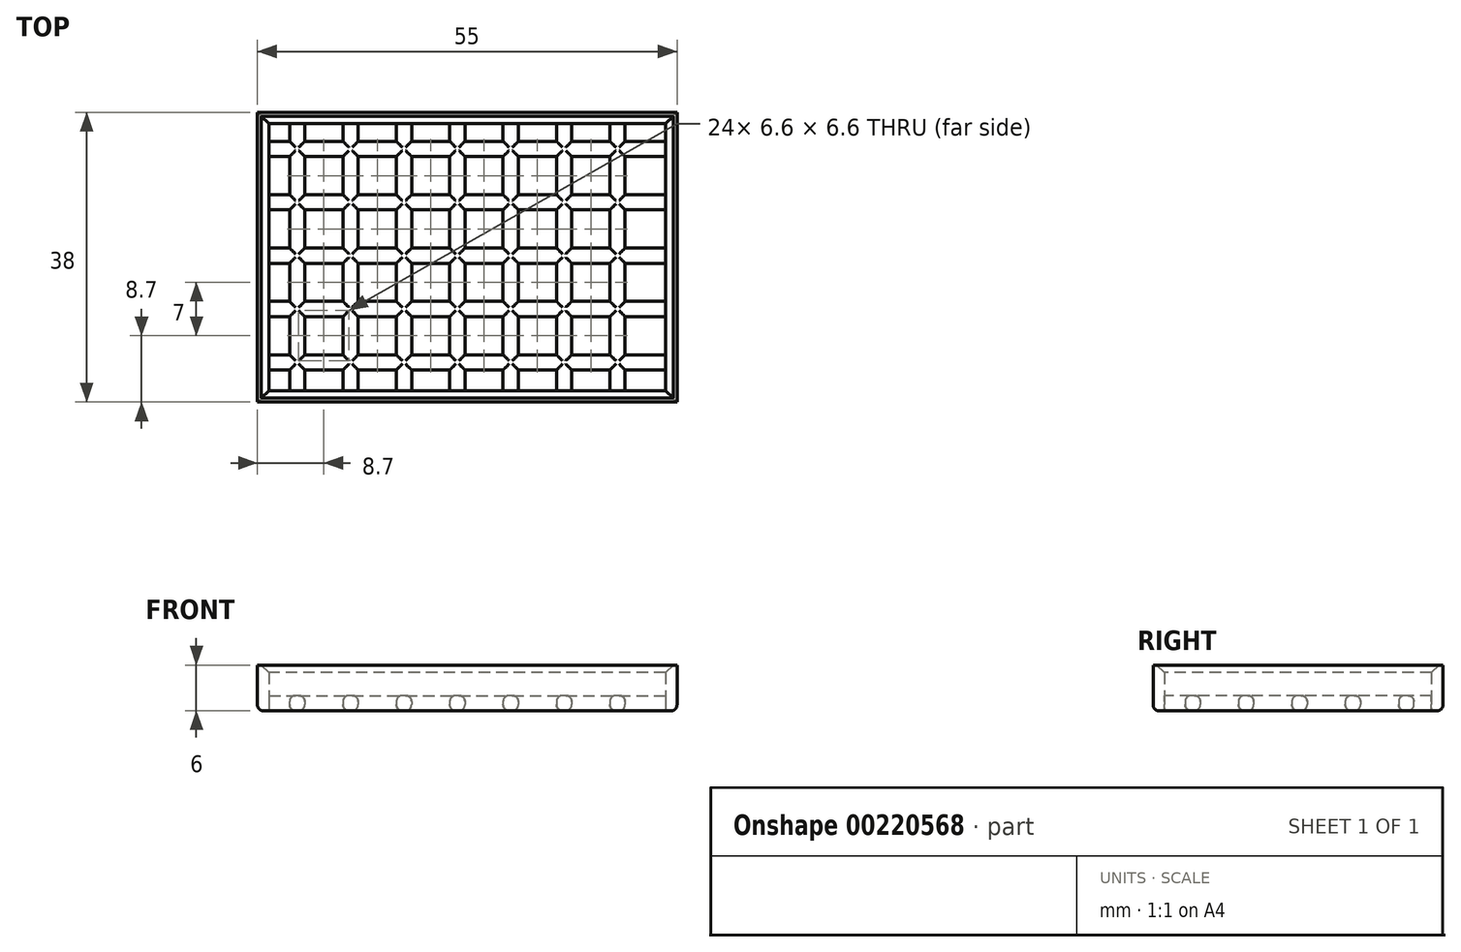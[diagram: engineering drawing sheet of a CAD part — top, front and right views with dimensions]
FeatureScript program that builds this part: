
annotation { "Feature Type Name" : "Feature", "Feature Type Description" : "" }
export const myFeature = defineFeature(function(context is Context, id is Id, definition is map)
    precondition{}
    {
        {
            var Q0;
            Q0=qCreatedBy(makeId("Top.planeOp"),FACE);
            var sketch = newSketch(context, id + "F0", { "sketchPlane" : qUnion([Q0])});
            skLineSegment(sketch, "E0.bottom", {"start": v(0, 38) * mm, "end": v(55, 38) * mm});
            skLineSegment(sketch, "E0.top", {"start": v(0, 0) * mm, "end": v(55, 0) * mm});
            skLineSegment(sketch, "E0.left", {"start": v(0, 38) * mm, "end": v(0, 0) * mm});
            skLineSegment(sketch, "E0.right", {"start": v(55, 38) * mm, "end": v(55, 0) * mm});
            skSolve(sketch);
        }
        {
            var Q0;
            Q0=qSketchRegion(id+"F0",true);
            extrude(context, id + "F1", {"entities" : qUnion([Q0]), "oppositeDirection" : true, "depth" : 2 * mm});
        }
        {
            var Q0;
            Q0=makeQuery(id+"F1.opExtrude","CAP_FACE",FACE,{"disambiguationData":[OSD([sQuery(id+"F0.wireOp",EDGE,"E0.bottom"),sQuery(id+"F0.wireOp",EDGE,"E0.top"),sQuery(id+"F0.wireOp",EDGE,"E0.left"),sQuery(id+"F0.wireOp",EDGE,"E0.right")])],"isStart":true});
            var sketch = newSketch(context, id + "F2", { "sketchPlane" : qUnion([Q0])});
            skLineSegment(sketch, "E1.bottom", {"start": v(-0.8, 39.2) * mm, "end": v(4.2, 39.2) * mm});
            skLineSegment(sketch, "E1.top", {"start": v(-0.8, 34.2) * mm, "end": v(4.2, 34.2) * mm});
            skLineSegment(sketch, "E1.left", {"start": v(-0.8, 39.2) * mm, "end": v(-0.8, 34.2) * mm});
            skLineSegment(sketch, "E1.right", {"start": v(4.2, 39.2) * mm, "end": v(4.2, 34.2) * mm});
            skLineSegment(sketch, "E2.0.1.0", {"start": v(-0.8, 32.2) * mm, "end": v(4.2, 32.2) * mm});
            skLineSegment(sketch, "E2.0.1.1", {"start": v(-0.8, 27.2) * mm, "end": v(4.2, 27.2) * mm});
            skLineSegment(sketch, "E2.0.1.2", {"start": v(-0.8, 32.2) * mm, "end": v(-0.8, 27.2) * mm});
            skLineSegment(sketch, "E2.0.1.3", {"start": v(4.2, 32.2) * mm, "end": v(4.2, 27.2) * mm});
            skLineSegment(sketch, "E2.0.2.0", {"start": v(-0.8, 25.2) * mm, "end": v(4.2, 25.2) * mm});
            skLineSegment(sketch, "E2.0.2.1", {"start": v(-0.8, 20.2) * mm, "end": v(4.2, 20.2) * mm});
            skLineSegment(sketch, "E2.0.2.2", {"start": v(-0.8, 25.2) * mm, "end": v(-0.8, 20.2) * mm});
            skLineSegment(sketch, "E2.0.2.3", {"start": v(4.2, 25.2) * mm, "end": v(4.2, 20.2) * mm});
            skLineSegment(sketch, "E2.0.3.0", {"start": v(-0.8, 18.2) * mm, "end": v(4.2, 18.2) * mm});
            skLineSegment(sketch, "E2.0.3.1", {"start": v(-0.8, 13.2) * mm, "end": v(4.2, 13.2) * mm});
            skLineSegment(sketch, "E2.0.3.2", {"start": v(-0.8, 18.2) * mm, "end": v(-0.8, 13.2) * mm});
            skLineSegment(sketch, "E2.0.3.3", {"start": v(4.2, 18.2) * mm, "end": v(4.2, 13.2) * mm});
            skLineSegment(sketch, "E2.0.4.0", {"start": v(-0.8, 11.2) * mm, "end": v(4.2, 11.2) * mm});
            skLineSegment(sketch, "E2.0.4.1", {"start": v(-0.8, 6.2) * mm, "end": v(4.2, 6.2) * mm});
            skLineSegment(sketch, "E2.0.4.2", {"start": v(-0.8, 11.2) * mm, "end": v(-0.8, 6.2) * mm});
            skLineSegment(sketch, "E2.0.4.3", {"start": v(4.2, 11.2) * mm, "end": v(4.2, 6.2) * mm});
            skLineSegment(sketch, "E2.0.5.0", {"start": v(-0.8, 4.2) * mm, "end": v(4.2, 4.2) * mm});
            skLineSegment(sketch, "E2.0.5.1", {"start": v(-0.8, -0.8) * mm, "end": v(4.2, -0.8) * mm});
            skLineSegment(sketch, "E2.0.5.2", {"start": v(-0.8, 4.2) * mm, "end": v(-0.8, -0.8) * mm});
            skLineSegment(sketch, "E2.0.5.3", {"start": v(4.2, 4.2) * mm, "end": v(4.2, -0.8) * mm});
            skLineSegment(sketch, "E2.1.0.0", {"start": v(6.2, 39.2) * mm, "end": v(11.2, 39.2) * mm});
            skLineSegment(sketch, "E2.1.0.1", {"start": v(6.2, 34.2) * mm, "end": v(11.2, 34.2) * mm});
            skLineSegment(sketch, "E2.1.0.2", {"start": v(6.2, 39.2) * mm, "end": v(6.2, 34.2) * mm});
            skLineSegment(sketch, "E2.1.0.3", {"start": v(11.2, 39.2) * mm, "end": v(11.2, 34.2) * mm});
            skLineSegment(sketch, "E2.1.1.0", {"start": v(6.2, 32.2) * mm, "end": v(11.2, 32.2) * mm});
            skLineSegment(sketch, "E2.1.1.1", {"start": v(6.2, 27.2) * mm, "end": v(11.2, 27.2) * mm});
            skLineSegment(sketch, "E2.1.1.2", {"start": v(6.2, 32.2) * mm, "end": v(6.2, 27.2) * mm});
            skLineSegment(sketch, "E2.1.1.3", {"start": v(11.2, 32.2) * mm, "end": v(11.2, 27.2) * mm});
            skLineSegment(sketch, "E2.1.2.0", {"start": v(6.2, 25.2) * mm, "end": v(11.2, 25.2) * mm});
            skLineSegment(sketch, "E2.1.2.1", {"start": v(6.2, 20.2) * mm, "end": v(11.2, 20.2) * mm});
            skLineSegment(sketch, "E2.1.2.2", {"start": v(6.2, 25.2) * mm, "end": v(6.2, 20.2) * mm});
            skLineSegment(sketch, "E2.1.2.3", {"start": v(11.2, 25.2) * mm, "end": v(11.2, 20.2) * mm});
            skLineSegment(sketch, "E2.1.3.0", {"start": v(6.2, 18.2) * mm, "end": v(11.2, 18.2) * mm});
            skLineSegment(sketch, "E2.1.3.1", {"start": v(6.2, 13.2) * mm, "end": v(11.2, 13.2) * mm});
            skLineSegment(sketch, "E2.1.3.2", {"start": v(6.2, 18.2) * mm, "end": v(6.2, 13.2) * mm});
            skLineSegment(sketch, "E2.1.3.3", {"start": v(11.2, 18.2) * mm, "end": v(11.2, 13.2) * mm});
            skLineSegment(sketch, "E2.1.4.0", {"start": v(6.2, 11.2) * mm, "end": v(11.2, 11.2) * mm});
            skLineSegment(sketch, "E2.1.4.1", {"start": v(6.2, 6.2) * mm, "end": v(11.2, 6.2) * mm});
            skLineSegment(sketch, "E2.1.4.2", {"start": v(6.2, 11.2) * mm, "end": v(6.2, 6.2) * mm});
            skLineSegment(sketch, "E2.1.4.3", {"start": v(11.2, 11.2) * mm, "end": v(11.2, 6.2) * mm});
            skLineSegment(sketch, "E2.1.5.0", {"start": v(6.2, 4.2) * mm, "end": v(11.2, 4.2) * mm});
            skLineSegment(sketch, "E2.1.5.1", {"start": v(6.2, -0.8) * mm, "end": v(11.2, -0.8) * mm});
            skLineSegment(sketch, "E2.1.5.2", {"start": v(6.2, 4.2) * mm, "end": v(6.2, -0.8) * mm});
            skLineSegment(sketch, "E2.1.5.3", {"start": v(11.2, 4.2) * mm, "end": v(11.2, -0.8) * mm});
            skLineSegment(sketch, "E2.2.0.0", {"start": v(13.2, 39.2) * mm, "end": v(18.2, 39.2) * mm});
            skLineSegment(sketch, "E2.2.0.1", {"start": v(13.2, 34.2) * mm, "end": v(18.2, 34.2) * mm});
            skLineSegment(sketch, "E2.2.0.2", {"start": v(13.2, 39.2) * mm, "end": v(13.2, 34.2) * mm});
            skLineSegment(sketch, "E2.2.0.3", {"start": v(18.2, 39.2) * mm, "end": v(18.2, 34.2) * mm});
            skLineSegment(sketch, "E2.2.1.0", {"start": v(13.2, 32.2) * mm, "end": v(18.2, 32.2) * mm});
            skLineSegment(sketch, "E2.2.1.1", {"start": v(13.2, 27.2) * mm, "end": v(18.2, 27.2) * mm});
            skLineSegment(sketch, "E2.2.1.2", {"start": v(13.2, 32.2) * mm, "end": v(13.2, 27.2) * mm});
            skLineSegment(sketch, "E2.2.1.3", {"start": v(18.2, 32.2) * mm, "end": v(18.2, 27.2) * mm});
            skLineSegment(sketch, "E2.2.2.0", {"start": v(13.2, 25.2) * mm, "end": v(18.2, 25.2) * mm});
            skLineSegment(sketch, "E2.2.2.1", {"start": v(13.2, 20.2) * mm, "end": v(18.2, 20.2) * mm});
            skLineSegment(sketch, "E2.2.2.2", {"start": v(13.2, 25.2) * mm, "end": v(13.2, 20.2) * mm});
            skLineSegment(sketch, "E2.2.2.3", {"start": v(18.2, 25.2) * mm, "end": v(18.2, 20.2) * mm});
            skLineSegment(sketch, "E2.2.3.0", {"start": v(13.2, 18.2) * mm, "end": v(18.2, 18.2) * mm});
            skLineSegment(sketch, "E2.2.3.1", {"start": v(13.2, 13.2) * mm, "end": v(18.2, 13.2) * mm});
            skLineSegment(sketch, "E2.2.3.2", {"start": v(13.2, 18.2) * mm, "end": v(13.2, 13.2) * mm});
            skLineSegment(sketch, "E2.2.3.3", {"start": v(18.2, 18.2) * mm, "end": v(18.2, 13.2) * mm});
            skLineSegment(sketch, "E2.2.4.0", {"start": v(13.2, 11.2) * mm, "end": v(18.2, 11.2) * mm});
            skLineSegment(sketch, "E2.2.4.1", {"start": v(13.2, 6.2) * mm, "end": v(18.2, 6.2) * mm});
            skLineSegment(sketch, "E2.2.4.2", {"start": v(13.2, 11.2) * mm, "end": v(13.2, 6.2) * mm});
            skLineSegment(sketch, "E2.2.4.3", {"start": v(18.2, 11.2) * mm, "end": v(18.2, 6.2) * mm});
            skLineSegment(sketch, "E2.2.5.0", {"start": v(13.2, 4.2) * mm, "end": v(18.2, 4.2) * mm});
            skLineSegment(sketch, "E2.2.5.1", {"start": v(13.2, -0.8) * mm, "end": v(18.2, -0.8) * mm});
            skLineSegment(sketch, "E2.2.5.2", {"start": v(13.2, 4.2) * mm, "end": v(13.2, -0.8) * mm});
            skLineSegment(sketch, "E2.2.5.3", {"start": v(18.2, 4.2) * mm, "end": v(18.2, -0.8) * mm});
            skLineSegment(sketch, "E2.3.0.0", {"start": v(20.2, 39.2) * mm, "end": v(25.2, 39.2) * mm});
            skLineSegment(sketch, "E2.3.0.1", {"start": v(20.2, 34.2) * mm, "end": v(25.2, 34.2) * mm});
            skLineSegment(sketch, "E2.3.0.2", {"start": v(20.2, 39.2) * mm, "end": v(20.2, 34.2) * mm});
            skLineSegment(sketch, "E2.3.0.3", {"start": v(25.2, 39.2) * mm, "end": v(25.2, 34.2) * mm});
            skLineSegment(sketch, "E2.3.1.0", {"start": v(20.2, 32.2) * mm, "end": v(25.2, 32.2) * mm});
            skLineSegment(sketch, "E2.3.1.1", {"start": v(20.2, 27.2) * mm, "end": v(25.2, 27.2) * mm});
            skLineSegment(sketch, "E2.3.1.2", {"start": v(20.2, 32.2) * mm, "end": v(20.2, 27.2) * mm});
            skLineSegment(sketch, "E2.3.1.3", {"start": v(25.2, 32.2) * mm, "end": v(25.2, 27.2) * mm});
            skLineSegment(sketch, "E2.3.2.0", {"start": v(20.2, 25.2) * mm, "end": v(25.2, 25.2) * mm});
            skLineSegment(sketch, "E2.3.2.1", {"start": v(20.2, 20.2) * mm, "end": v(25.2, 20.2) * mm});
            skLineSegment(sketch, "E2.3.2.2", {"start": v(20.2, 25.2) * mm, "end": v(20.2, 20.2) * mm});
            skLineSegment(sketch, "E2.3.2.3", {"start": v(25.2, 25.2) * mm, "end": v(25.2, 20.2) * mm});
            skLineSegment(sketch, "E2.3.3.0", {"start": v(20.2, 18.2) * mm, "end": v(25.2, 18.2) * mm});
            skLineSegment(sketch, "E2.3.3.1", {"start": v(20.2, 13.2) * mm, "end": v(25.2, 13.2) * mm});
            skLineSegment(sketch, "E2.3.3.2", {"start": v(20.2, 18.2) * mm, "end": v(20.2, 13.2) * mm});
            skLineSegment(sketch, "E2.3.3.3", {"start": v(25.2, 18.2) * mm, "end": v(25.2, 13.2) * mm});
            skLineSegment(sketch, "E2.3.4.0", {"start": v(20.2, 11.2) * mm, "end": v(25.2, 11.2) * mm});
            skLineSegment(sketch, "E2.3.4.1", {"start": v(20.2, 6.2) * mm, "end": v(25.2, 6.2) * mm});
            skLineSegment(sketch, "E2.3.4.2", {"start": v(20.2, 11.2) * mm, "end": v(20.2, 6.2) * mm});
            skLineSegment(sketch, "E2.3.4.3", {"start": v(25.2, 11.2) * mm, "end": v(25.2, 6.2) * mm});
            skLineSegment(sketch, "E2.3.5.0", {"start": v(20.2, 4.2) * mm, "end": v(25.2, 4.2) * mm});
            skLineSegment(sketch, "E2.3.5.1", {"start": v(20.2, -0.8) * mm, "end": v(25.2, -0.8) * mm});
            skLineSegment(sketch, "E2.3.5.2", {"start": v(20.2, 4.2) * mm, "end": v(20.2, -0.8) * mm});
            skLineSegment(sketch, "E2.3.5.3", {"start": v(25.2, 4.2) * mm, "end": v(25.2, -0.8) * mm});
            skLineSegment(sketch, "E2.4.0.0", {"start": v(27.2, 39.2) * mm, "end": v(32.2, 39.2) * mm});
            skLineSegment(sketch, "E2.4.0.1", {"start": v(27.2, 34.2) * mm, "end": v(32.2, 34.2) * mm});
            skLineSegment(sketch, "E2.4.0.2", {"start": v(27.2, 39.2) * mm, "end": v(27.2, 34.2) * mm});
            skLineSegment(sketch, "E2.4.0.3", {"start": v(32.2, 39.2) * mm, "end": v(32.2, 34.2) * mm});
            skLineSegment(sketch, "E2.4.1.0", {"start": v(27.2, 32.2) * mm, "end": v(32.2, 32.2) * mm});
            skLineSegment(sketch, "E2.4.1.1", {"start": v(27.2, 27.2) * mm, "end": v(32.2, 27.2) * mm});
            skLineSegment(sketch, "E2.4.1.2", {"start": v(27.2, 32.2) * mm, "end": v(27.2, 27.2) * mm});
            skLineSegment(sketch, "E2.4.1.3", {"start": v(32.2, 32.2) * mm, "end": v(32.2, 27.2) * mm});
            skLineSegment(sketch, "E2.4.2.0", {"start": v(27.2, 25.2) * mm, "end": v(32.2, 25.2) * mm});
            skLineSegment(sketch, "E2.4.2.1", {"start": v(27.2, 20.2) * mm, "end": v(32.2, 20.2) * mm});
            skLineSegment(sketch, "E2.4.2.2", {"start": v(27.2, 25.2) * mm, "end": v(27.2, 20.2) * mm});
            skLineSegment(sketch, "E2.4.2.3", {"start": v(32.2, 25.2) * mm, "end": v(32.2, 20.2) * mm});
            skLineSegment(sketch, "E2.4.3.0", {"start": v(27.2, 18.2) * mm, "end": v(32.2, 18.2) * mm});
            skLineSegment(sketch, "E2.4.3.1", {"start": v(27.2, 13.2) * mm, "end": v(32.2, 13.2) * mm});
            skLineSegment(sketch, "E2.4.3.2", {"start": v(27.2, 18.2) * mm, "end": v(27.2, 13.2) * mm});
            skLineSegment(sketch, "E2.4.3.3", {"start": v(32.2, 18.2) * mm, "end": v(32.2, 13.2) * mm});
            skLineSegment(sketch, "E2.4.4.0", {"start": v(27.2, 11.2) * mm, "end": v(32.2, 11.2) * mm});
            skLineSegment(sketch, "E2.4.4.1", {"start": v(27.2, 6.2) * mm, "end": v(32.2, 6.2) * mm});
            skLineSegment(sketch, "E2.4.4.2", {"start": v(27.2, 11.2) * mm, "end": v(27.2, 6.2) * mm});
            skLineSegment(sketch, "E2.4.4.3", {"start": v(32.2, 11.2) * mm, "end": v(32.2, 6.2) * mm});
            skLineSegment(sketch, "E2.4.5.0", {"start": v(27.2, 4.2) * mm, "end": v(32.2, 4.2) * mm});
            skLineSegment(sketch, "E2.4.5.1", {"start": v(27.2, -0.8) * mm, "end": v(32.2, -0.8) * mm});
            skLineSegment(sketch, "E2.4.5.2", {"start": v(27.2, 4.2) * mm, "end": v(27.2, -0.8) * mm});
            skLineSegment(sketch, "E2.4.5.3", {"start": v(32.2, 4.2) * mm, "end": v(32.2, -0.8) * mm});
            skLineSegment(sketch, "E2.5.0.0", {"start": v(34.2, 39.2) * mm, "end": v(39.2, 39.2) * mm});
            skLineSegment(sketch, "E2.5.0.1", {"start": v(34.2, 34.2) * mm, "end": v(39.2, 34.2) * mm});
            skLineSegment(sketch, "E2.5.0.2", {"start": v(34.2, 39.2) * mm, "end": v(34.2, 34.2) * mm});
            skLineSegment(sketch, "E2.5.0.3", {"start": v(39.2, 39.2) * mm, "end": v(39.2, 34.2) * mm});
            skLineSegment(sketch, "E2.5.1.0", {"start": v(34.2, 32.2) * mm, "end": v(39.2, 32.2) * mm});
            skLineSegment(sketch, "E2.5.1.1", {"start": v(34.2, 27.2) * mm, "end": v(39.2, 27.2) * mm});
            skLineSegment(sketch, "E2.5.1.2", {"start": v(34.2, 32.2) * mm, "end": v(34.2, 27.2) * mm});
            skLineSegment(sketch, "E2.5.1.3", {"start": v(39.2, 32.2) * mm, "end": v(39.2, 27.2) * mm});
            skLineSegment(sketch, "E2.5.2.0", {"start": v(34.2, 25.2) * mm, "end": v(39.2, 25.2) * mm});
            skLineSegment(sketch, "E2.5.2.1", {"start": v(34.2, 20.2) * mm, "end": v(39.2, 20.2) * mm});
            skLineSegment(sketch, "E2.5.2.2", {"start": v(34.2, 25.2) * mm, "end": v(34.2, 20.2) * mm});
            skLineSegment(sketch, "E2.5.2.3", {"start": v(39.2, 25.2) * mm, "end": v(39.2, 20.2) * mm});
            skLineSegment(sketch, "E2.5.3.0", {"start": v(34.2, 18.2) * mm, "end": v(39.2, 18.2) * mm});
            skLineSegment(sketch, "E2.5.3.1", {"start": v(34.2, 13.2) * mm, "end": v(39.2, 13.2) * mm});
            skLineSegment(sketch, "E2.5.3.2", {"start": v(34.2, 18.2) * mm, "end": v(34.2, 13.2) * mm});
            skLineSegment(sketch, "E2.5.3.3", {"start": v(39.2, 18.2) * mm, "end": v(39.2, 13.2) * mm});
            skLineSegment(sketch, "E2.5.4.0", {"start": v(34.2, 11.2) * mm, "end": v(39.2, 11.2) * mm});
            skLineSegment(sketch, "E2.5.4.1", {"start": v(34.2, 6.2) * mm, "end": v(39.2, 6.2) * mm});
            skLineSegment(sketch, "E2.5.4.2", {"start": v(34.2, 11.2) * mm, "end": v(34.2, 6.2) * mm});
            skLineSegment(sketch, "E2.5.4.3", {"start": v(39.2, 11.2) * mm, "end": v(39.2, 6.2) * mm});
            skLineSegment(sketch, "E2.5.5.0", {"start": v(34.2, 4.2) * mm, "end": v(39.2, 4.2) * mm});
            skLineSegment(sketch, "E2.5.5.1", {"start": v(34.2, -0.8) * mm, "end": v(39.2, -0.8) * mm});
            skLineSegment(sketch, "E2.5.5.2", {"start": v(34.2, 4.2) * mm, "end": v(34.2, -0.8) * mm});
            skLineSegment(sketch, "E2.5.5.3", {"start": v(39.2, 4.2) * mm, "end": v(39.2, -0.8) * mm});
            skLineSegment(sketch, "E2.6.0.0", {"start": v(41.2, 39.2) * mm, "end": v(46.2, 39.2) * mm});
            skLineSegment(sketch, "E2.6.0.1", {"start": v(41.2, 34.2) * mm, "end": v(46.2, 34.2) * mm});
            skLineSegment(sketch, "E2.6.0.2", {"start": v(41.2, 39.2) * mm, "end": v(41.2, 34.2) * mm});
            skLineSegment(sketch, "E2.6.0.3", {"start": v(46.2, 39.2) * mm, "end": v(46.2, 34.2) * mm});
            skLineSegment(sketch, "E2.6.1.0", {"start": v(41.2, 32.2) * mm, "end": v(46.2, 32.2) * mm});
            skLineSegment(sketch, "E2.6.1.1", {"start": v(41.2, 27.2) * mm, "end": v(46.2, 27.2) * mm});
            skLineSegment(sketch, "E2.6.1.2", {"start": v(41.2, 32.2) * mm, "end": v(41.2, 27.2) * mm});
            skLineSegment(sketch, "E2.6.1.3", {"start": v(46.2, 32.2) * mm, "end": v(46.2, 27.2) * mm});
            skLineSegment(sketch, "E2.6.2.0", {"start": v(41.2, 25.2) * mm, "end": v(46.2, 25.2) * mm});
            skLineSegment(sketch, "E2.6.2.1", {"start": v(41.2, 20.2) * mm, "end": v(46.2, 20.2) * mm});
            skLineSegment(sketch, "E2.6.2.2", {"start": v(41.2, 25.2) * mm, "end": v(41.2, 20.2) * mm});
            skLineSegment(sketch, "E2.6.2.3", {"start": v(46.2, 25.2) * mm, "end": v(46.2, 20.2) * mm});
            skLineSegment(sketch, "E2.6.3.0", {"start": v(41.2, 18.2) * mm, "end": v(46.2, 18.2) * mm});
            skLineSegment(sketch, "E2.6.3.1", {"start": v(41.2, 13.2) * mm, "end": v(46.2, 13.2) * mm});
            skLineSegment(sketch, "E2.6.3.2", {"start": v(41.2, 18.2) * mm, "end": v(41.2, 13.2) * mm});
            skLineSegment(sketch, "E2.6.3.3", {"start": v(46.2, 18.2) * mm, "end": v(46.2, 13.2) * mm});
            skLineSegment(sketch, "E2.6.4.0", {"start": v(41.2, 11.2) * mm, "end": v(46.2, 11.2) * mm});
            skLineSegment(sketch, "E2.6.4.1", {"start": v(41.2, 6.2) * mm, "end": v(46.2, 6.2) * mm});
            skLineSegment(sketch, "E2.6.4.2", {"start": v(41.2, 11.2) * mm, "end": v(41.2, 6.2) * mm});
            skLineSegment(sketch, "E2.6.4.3", {"start": v(46.2, 11.2) * mm, "end": v(46.2, 6.2) * mm});
            skLineSegment(sketch, "E2.6.5.0", {"start": v(41.2, 4.2) * mm, "end": v(46.2, 4.2) * mm});
            skLineSegment(sketch, "E2.6.5.1", {"start": v(41.2, -0.8) * mm, "end": v(46.2, -0.8) * mm});
            skLineSegment(sketch, "E2.6.5.2", {"start": v(41.2, 4.2) * mm, "end": v(41.2, -0.8) * mm});
            skLineSegment(sketch, "E2.6.5.3", {"start": v(46.2, 4.2) * mm, "end": v(46.2, -0.8) * mm});
            skLineSegment(sketch, "E2.7.0.0", {"start": v(48.2, 39.2) * mm, "end": v(53.2, 39.2) * mm});
            skLineSegment(sketch, "E2.7.0.1", {"start": v(48.2, 34.2) * mm, "end": v(53.2, 34.2) * mm});
            skLineSegment(sketch, "E2.7.0.2", {"start": v(48.2, 39.2) * mm, "end": v(48.2, 34.2) * mm});
            skLineSegment(sketch, "E2.7.0.3", {"start": v(53.2, 39.2) * mm, "end": v(53.2, 34.2) * mm});
            skLineSegment(sketch, "E2.7.1.0", {"start": v(48.2, 32.2) * mm, "end": v(53.2, 32.2) * mm});
            skLineSegment(sketch, "E2.7.1.1", {"start": v(48.2, 27.2) * mm, "end": v(53.2, 27.2) * mm});
            skLineSegment(sketch, "E2.7.1.2", {"start": v(48.2, 32.2) * mm, "end": v(48.2, 27.2) * mm});
            skLineSegment(sketch, "E2.7.1.3", {"start": v(53.2, 32.2) * mm, "end": v(53.2, 27.2) * mm});
            skLineSegment(sketch, "E2.7.2.0", {"start": v(48.2, 25.2) * mm, "end": v(53.2, 25.2) * mm});
            skLineSegment(sketch, "E2.7.2.1", {"start": v(48.2, 20.2) * mm, "end": v(53.2, 20.2) * mm});
            skLineSegment(sketch, "E2.7.2.2", {"start": v(48.2, 25.2) * mm, "end": v(48.2, 20.2) * mm});
            skLineSegment(sketch, "E2.7.2.3", {"start": v(53.2, 25.2) * mm, "end": v(53.2, 20.2) * mm});
            skLineSegment(sketch, "E2.7.3.0", {"start": v(48.2, 18.2) * mm, "end": v(53.2, 18.2) * mm});
            skLineSegment(sketch, "E2.7.3.1", {"start": v(48.2, 13.2) * mm, "end": v(53.2, 13.2) * mm});
            skLineSegment(sketch, "E2.7.3.2", {"start": v(48.2, 18.2) * mm, "end": v(48.2, 13.2) * mm});
            skLineSegment(sketch, "E2.7.3.3", {"start": v(53.2, 18.2) * mm, "end": v(53.2, 13.2) * mm});
            skLineSegment(sketch, "E2.7.4.0", {"start": v(48.2, 11.2) * mm, "end": v(53.2, 11.2) * mm});
            skLineSegment(sketch, "E2.7.4.1", {"start": v(48.2, 6.2) * mm, "end": v(53.2, 6.2) * mm});
            skLineSegment(sketch, "E2.7.4.2", {"start": v(48.2, 11.2) * mm, "end": v(48.2, 6.2) * mm});
            skLineSegment(sketch, "E2.7.4.3", {"start": v(53.2, 11.2) * mm, "end": v(53.2, 6.2) * mm});
            skLineSegment(sketch, "E2.7.5.0", {"start": v(48.2, 4.2) * mm, "end": v(53.2, 4.2) * mm});
            skLineSegment(sketch, "E2.7.5.1", {"start": v(48.2, -0.8) * mm, "end": v(53.2, -0.8) * mm});
            skLineSegment(sketch, "E2.7.5.2", {"start": v(48.2, 4.2) * mm, "end": v(48.2, -0.8) * mm});
            skLineSegment(sketch, "E2.7.5.3", {"start": v(53.2, 4.2) * mm, "end": v(53.2, -0.8) * mm});
            skLineSegment(sketch, "E2.direction1", {"start": v(-0.8, 34.2) * mm, "end": v(6.2, 34.2) * mm, "construction": true});
            skLineSegment(sketch, "E2.direction2", {"start": v(-0.8, 34.2) * mm, "end": v(-0.8, 27.2) * mm, "construction": true});
            skLineSegment(sketch, "E3.bottom", {"start": v(53.2, 39.2) * mm, "end": v(57.35, 39.2) * mm});
            skLineSegment(sketch, "E3.top", {"start": v(53.2, 34.2) * mm, "end": v(57.35, 34.2) * mm});
            skLineSegment(sketch, "E3.right", {"start": v(57.35, 39.2) * mm, "end": v(57.35, 34.2) * mm});
            skLineSegment(sketch, "E4.1.0.0", {"start": v(53.2, 27.2) * mm, "end": v(57.35, 27.2) * mm});
            skLineSegment(sketch, "E4.1.0.1", {"start": v(57.35, 32.2) * mm, "end": v(57.35, 27.2) * mm});
            skLineSegment(sketch, "E4.1.0.2", {"start": v(53.2, 32.2) * mm, "end": v(57.35, 32.2) * mm});
            skLineSegment(sketch, "E4.2.0.0", {"start": v(53.2, 20.2) * mm, "end": v(57.35, 20.2) * mm});
            skLineSegment(sketch, "E4.2.0.1", {"start": v(57.35, 25.2) * mm, "end": v(57.35, 20.2) * mm});
            skLineSegment(sketch, "E4.2.0.2", {"start": v(53.2, 25.2) * mm, "end": v(57.35, 25.2) * mm});
            skLineSegment(sketch, "E4.3.0.0", {"start": v(53.2, 13.2) * mm, "end": v(57.35, 13.2) * mm});
            skLineSegment(sketch, "E4.3.0.1", {"start": v(57.35, 18.2) * mm, "end": v(57.35, 13.2) * mm});
            skLineSegment(sketch, "E4.3.0.2", {"start": v(53.2, 18.2) * mm, "end": v(57.35, 18.2) * mm});
            skLineSegment(sketch, "E4.4.0.0", {"start": v(53.2, 6.2) * mm, "end": v(57.35, 6.2) * mm});
            skLineSegment(sketch, "E4.4.0.1", {"start": v(57.35, 11.2) * mm, "end": v(57.35, 6.2) * mm});
            skLineSegment(sketch, "E4.4.0.2", {"start": v(53.2, 11.2) * mm, "end": v(57.35, 11.2) * mm});
            skLineSegment(sketch, "E4.5.0.0", {"start": v(53.2, -0.8) * mm, "end": v(57.35, -0.8) * mm});
            skLineSegment(sketch, "E4.5.0.1", {"start": v(57.35, 4.2) * mm, "end": v(57.35, -0.8) * mm});
            skLineSegment(sketch, "E4.5.0.2", {"start": v(53.2, 4.2) * mm, "end": v(57.35, 4.2) * mm});
            skLineSegment(sketch, "E4.direction1", {"start": v(53.2, 34.2) * mm, "end": v(53.2, 27.2) * mm, "construction": true});
            skSolve(sketch);
        }
        {
            var Q0;
            Q0=qSketchRegion(id+"F2",true);
            extrude(context, id + "F3", {"entities" : qUnion([Q0]), "operationType" : NewBodyOperationType.REMOVE, "endBound" : BoundingType.THROUGH_ALL, "oppositeDirection" : true, "depth" : 25 * mm});
        }
        {
            var Q0;
            Q0=makeQuery(id+"F1.opExtrude","CAP_FACE",FACE,{"disambiguationData":[OSD([sQuery(id+"F0.wireOp",EDGE,"E0.bottom"),sQuery(id+"F0.wireOp",EDGE,"E0.top"),sQuery(id+"F0.wireOp",EDGE,"E0.left"),sQuery(id+"F0.wireOp",EDGE,"E0.right")])],"isStart":false});
            var sketch = newSketch(context, id + "F4", { "sketchPlane" : qUnion([Q0])});
            skLineSegment(sketch, "E5.bottom", {"start": v(0, 0) * mm, "end": v(55, 0) * mm});
            skLineSegment(sketch, "E5.top", {"start": v(0, -38) * mm, "end": v(55, -38) * mm});
            skLineSegment(sketch, "E5.left", {"start": v(0, 0) * mm, "end": v(0, -38) * mm});
            skLineSegment(sketch, "E5.right", {"start": v(55, 0) * mm, "end": v(55, -38) * mm});
            skLineSegment(sketch, "E6.0", {"start": v(1.5, -1.5) * mm, "end": v(1.5, -36.5) * mm});
            skLineSegment(sketch, "E6.1", {"start": v(1.5, -1.5) * mm, "end": v(53.5, -1.5) * mm});
            skLineSegment(sketch, "E6.2", {"start": v(53.5, -1.5) * mm, "end": v(53.5, -36.5) * mm});
            skLineSegment(sketch, "E6.3", {"start": v(1.5, -36.5) * mm, "end": v(53.5, -36.5) * mm});
            skSolve(sketch);
        }
        {
            var Q0;
            Q0=makeQuery(id+"F1.opExtrude","CAP_FACE",FACE,{"disambiguationData":[OSD([sQuery(id+"F0.wireOp",EDGE,"E0.bottom"),sQuery(id+"F0.wireOp",EDGE,"E0.top"),sQuery(id+"F0.wireOp",EDGE,"E0.left"),sQuery(id+"F0.wireOp",EDGE,"E0.right")])],"isStart":true});
            var Q1;
            Q1=makeQuery(id+"F1.opExtrude","CAP_FACE",FACE,{"disambiguationData":[OSD([sQuery(id+"F0.wireOp",EDGE,"E0.bottom"),sQuery(id+"F0.wireOp",EDGE,"E0.top"),sQuery(id+"F0.wireOp",EDGE,"E0.left"),sQuery(id+"F0.wireOp",EDGE,"E0.right")])],"isStart":false});
            fillet(context, id + "F5", {"entities" : qUnion([Q0, Q1]), "radius" : 0.8 * mm, "defaultsChanged" : true, "vertexSettings" : [], "allowEdgeOverflow" : false});
        }
        {
            var Q0;
            Q0=qSketchRegion(id+"F4",true);
            extrude(context, id + "F6", {"entities" : qUnion([Q0]), "operationType" : NewBodyOperationType.ADD, "oppositeDirection" : true, "depth" : 6 * mm});
        }
        {
            var Q0;
            Q0=makeQuery(id+"F6.opExtrude","CAP_EDGE",EDGE,{"disambiguationData":[OSD([sQuery(id+"F4.wireOp",EDGE,"E5.left")])],"isStart":true});
            var Q1;
            Q1=makeQuery(id+"F6.opExtrude","CAP_EDGE",EDGE,{"disambiguationData":[OSD([sQuery(id+"F4.wireOp",EDGE,"E5.bottom")])],"isStart":true});
            var Q2;
            Q2=makeQuery(id+"F6.opExtrude","CAP_EDGE",EDGE,{"disambiguationData":[OSD([sQuery(id+"F4.wireOp",EDGE,"E5.right")])],"isStart":true});
            var Q3;
            Q3=makeQuery(id+"F6.opExtrude","CAP_EDGE",EDGE,{"disambiguationData":[OSD([sQuery(id+"F4.wireOp",EDGE,"E5.top")])],"isStart":true});
            fillet(context, id + "F7", {"entities" : qUnion([Q0, Q1, Q2, Q3]), "radius" : 0.75 * mm, "tangentPropagation" : true, "allowEdgeOverflow" : false});
        }
        {
            var Q0;
            Q0=makeQuery(id+"F6.opExtrude","CAP_EDGE",EDGE,{"disambiguationData":[OSD([sQuery(id+"F4.wireOp",EDGE,"E6.3")])],"isStart":false});
            var Q1;
            Q1=makeQuery(id+"F6.opExtrude","CAP_EDGE",EDGE,{"disambiguationData":[OSD([sQuery(id+"F4.wireOp",EDGE,"E6.0")])],"isStart":false});
            var Q2;
            Q2=makeQuery(id+"F6.opExtrude","CAP_EDGE",EDGE,{"disambiguationData":[OSD([sQuery(id+"F4.wireOp",EDGE,"E6.1")])],"isStart":false});
            var Q3;
            Q3=makeQuery(id+"F6.opExtrude","CAP_EDGE",EDGE,{"disambiguationData":[OSD([sQuery(id+"F4.wireOp",EDGE,"E6.2")])],"isStart":false});
            chamfer(context, id + "F8", {"entities" : qUnion([Q0, Q1, Q2, Q3]), "width" : 1 * mm, "tangentPropagation" : true});
        }
    });
